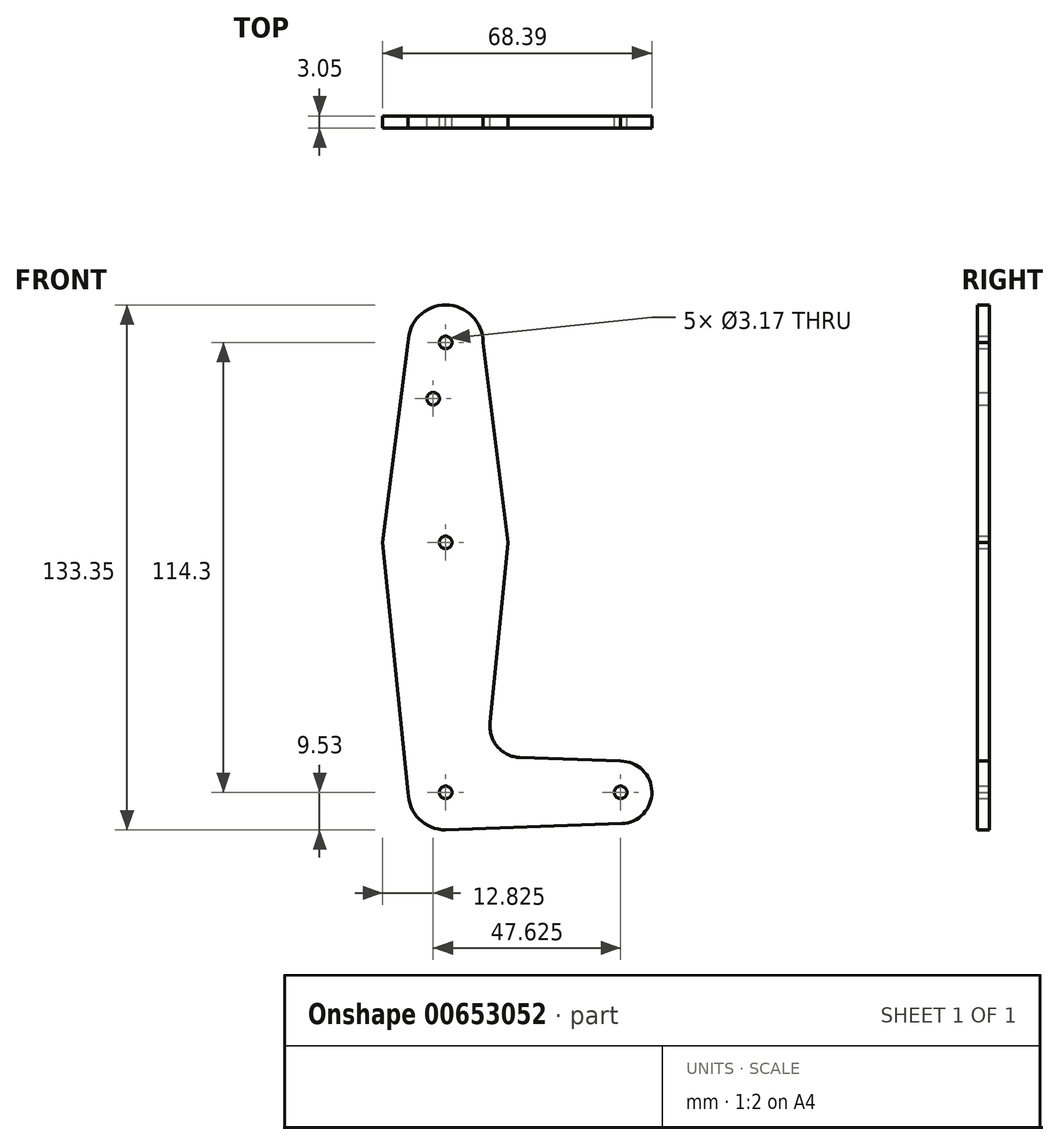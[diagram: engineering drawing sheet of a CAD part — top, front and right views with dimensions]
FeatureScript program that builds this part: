
annotation { "Feature Type Name" : "Feature", "Feature Type Description" : "" }
export const myFeature = defineFeature(function(context is Context, id is Id, definition is map)
    precondition{}
    {
        {
            var Q0;
            Q0=qCreatedBy(makeId("Front.planeOp"),FACE);
            var sketch = newSketch(context, id + "F0", { "sketchPlane" : qUnion([Q0])});
            skCircle(sketch, "E0", {"center": v(0, 50.8) * mm, "radius": 9.53 * mm});
            skCircle(sketch, "E1", {"center": v(0, 0) * mm, "radius": 15.88 * mm});
            skCircle(sketch, "E2", {"center": v(0, -63.5) * mm, "radius": 9.53 * mm});
            skCircle(sketch, "E3", {"center": v(44.45, -63.5) * mm, "radius": 7.94 * mm});
            skLineSegment(sketch, "E4", {"start": v(15.88, 0) * mm, "end": v(9.53, 50.8) * mm});
            skLineSegment(sketch, "E5", {"start": v(-9.52, 50.8) * mm, "end": v(-16, 0) * mm});
            skLineSegment(sketch, "E6", {"start": v(15.88, 0) * mm, "end": v(11.28, -45.91) * mm});
            skLineSegment(sketch, "E7", {"start": v(18.91, -54.65) * mm, "end": v(44.45, -55.56) * mm});
            skLineSegment(sketch, "E8", {"start": v(0, -73.03) * mm, "end": v(44.73, -71.43) * mm});
            skPoint(sketch, "E9.orphan", {"position": v(9.53, -63.5) * mm});
            skPoint(sketch, "E10.orphan", {"position": v(0, -53.98) * mm});
            skPoint(sketch, "E11.visualSharp", {"position": v(10.44, -54.35) * mm});
            skArc(sketch, "E11.filletArc", {"start": v(11.28, -45.91) * mm, "mid": v(13.2, -51.93) * mm, "end": v(18.91, -54.65) * mm});
            skCircle(sketch, "E12", {"center": v(0, 50.8) * mm, "radius": 1.59 * mm});
            skCircle(sketch, "E13", {"center": v(0, 0) * mm, "radius": 1.59 * mm});
            skCircle(sketch, "E14", {"center": v(0, -63.5) * mm, "radius": 1.59 * mm});
            skCircle(sketch, "E15", {"center": v(44.45, -63.5) * mm, "radius": 1.59 * mm});
            skCircle(sketch, "E16", {"center": v(-3.18, 36.53) * mm, "radius": 1.59 * mm});
            skLineSegment(sketch, "E17", {"start": v(-16, 0) * mm, "end": v(-9.52, -63.5) * mm});
            skSolve(sketch);
        }
        {
            var Q0;
            Q0=makeQuery(id+"F0.imprint","IMPRINT",FACE,{"disambiguationData":[TD([[makeQuery(id+"F0.imprint","IMPRINT",EDGE,{"derivedFrom":sQuery(id+"F0.wireOp",EDGE,"E12")}),-1.0]])]});
            var Q1;
            Q1=makeQuery(id+"F0.imprint","IMPRINT",FACE,{"disambiguationData":[TD([[makeQuery(id+"F0.imprint","IMPRINT",EDGE,{"derivedFrom":sQuery(id+"F0.wireOp",EDGE,"E16")}),-1.0]])]});
            var Q2;
            Q2=makeQuery(id+"F0.imprint","IMPRINT",FACE,{"disambiguationData":[TD([[makeQuery(id+"F0.imprint","IMPRINT",EDGE,{"derivedFrom":sQuery(id+"F0.wireOp",EDGE,"E13")}),-1.0]])]});
            var Q3;
            {var subQ9=sQuery(id+"F0.wireOp",EDGE,"E7");Q3=makeQuery(id+"F0.imprint","IMPRINT",FACE,{"disambiguationData":[TD([[makeQuery(id+"F0.imprint","IMPRINT",EDGE,{"derivedFrom":subQ9}),-1.0]])]});}
            var Q4;
            Q4=makeQuery(id+"F0.imprint","IMPRINT",FACE,{"disambiguationData":[TD([[makeQuery(id+"F0.imprint","IMPRINT",EDGE,{"derivedFrom":sQuery(id+"F0.wireOp",EDGE,"E15")}),-1.0]])]});
            var Q5;
            Q5=makeQuery(id+"F0.imprint","IMPRINT",FACE,{"disambiguationData":[TD([[makeQuery(id+"F0.imprint","IMPRINT",EDGE,{"derivedFrom":sQuery(id+"F0.wireOp",EDGE,"E14")}),-1.0]])]});
            extrude(context, id + "F1", {"entities" : qUnion([Q0, Q1, Q2, Q3, Q4, Q5]), "depth" : 3.05 * mm, "offsetDistance" : 25.4 * mm});
        }
    });
